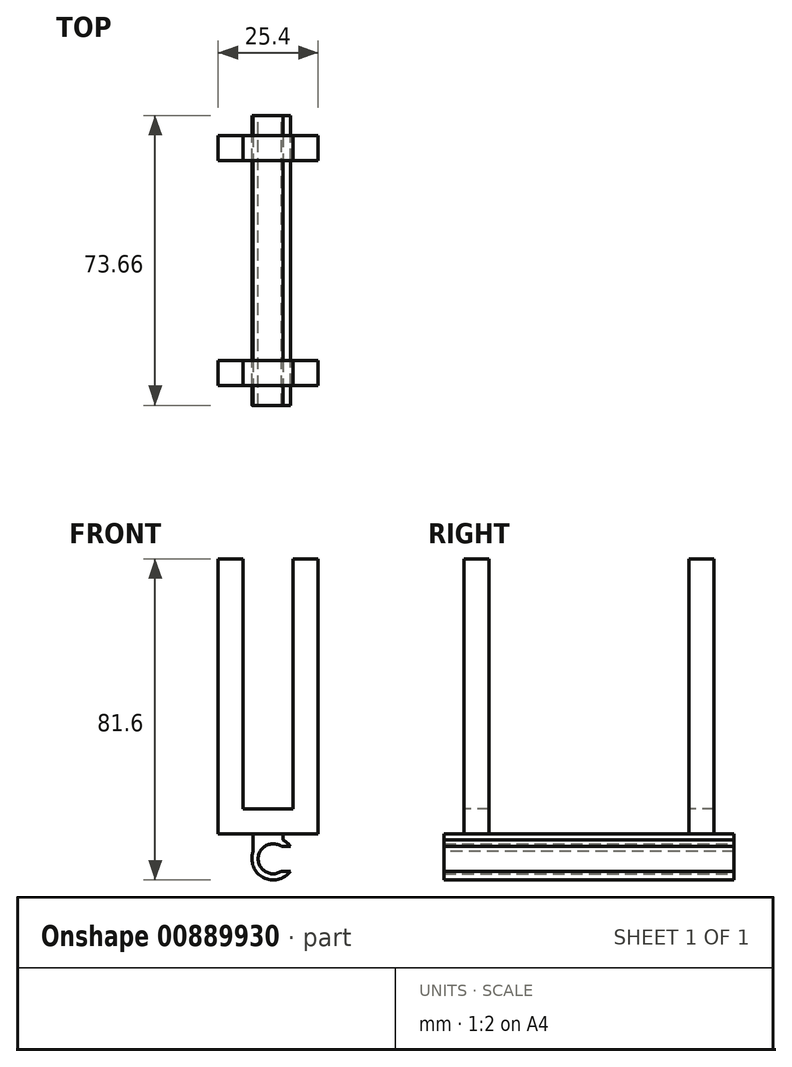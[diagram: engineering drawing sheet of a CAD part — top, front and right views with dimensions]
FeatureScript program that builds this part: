
annotation { "Feature Type Name" : "Feature", "Feature Type Description" : "" }
export const myFeature = defineFeature(function(context is Context, id is Id, definition is map)
    precondition{}
    {
        {
            var Q0;
            Q0=qCreatedBy(makeId("Front.planeOp"),FACE);
            var sketch = newSketch(context, id + "F0", { "sketchPlane" : qUnion([Q0])});
            skArc(sketch, "E0", {"start": v(2.1, 3.18) * mm, "mid": v(-3.81, 0) * mm, "end": v(2.1, -3.18) * mm});
            skArc(sketch, "E1.0", {"start": v(4.36, 3.18) * mm, "mid": v(-5.4, 0) * mm, "end": v(4.36, -3.18) * mm});
            skLineSegment(sketch, "E2", {"start": v(-5.4, 0) * mm, "end": v(5.4, 0) * mm, "construction": true});
            skLineSegment(sketch, "E3", {"start": v(-6.63, 3.18) * mm, "end": v(7.37, 3.18) * mm, "construction": true});
            skLineSegment(sketch, "E4", {"start": v(-6.34, -3.18) * mm, "end": v(7.33, -3.18) * mm, "construction": true});
            skLineSegment(sketch, "E5", {"start": v(2.1, 3.18) * mm, "end": v(4.36, 3.18) * mm});
            skLineSegment(sketch, "E6", {"start": v(2.1, -3.18) * mm, "end": v(4.36, -3.18) * mm});
            skPoint(sketch, "E6.startSnap0", {"position": v(0.5, -3.18) * mm});
            skSolve(sketch);
        }
        {
            var Q0;
            Q0 = qSketchRegion(id + "F0", true);
            extrude(context, id + "F1", {"entities" : qUnion([Q0]), "depth" : 73.66 * mm, "offsetDistance" : 25.4 * mm});
        }
        {
            var Q0;
            Q0=makeQuery(id+"F1.opExtrude","CAP_FACE",FACE,{"disambiguationData":[OSD([sQuery(id+"F0.wireOp",EDGE,"E0"),sQuery(id+"F0.wireOp",EDGE,"E1.0"),sQuery(id+"F0.wireOp",EDGE,"E5"),sQuery(id+"F0.wireOp",EDGE,"E6")])],"isStart":false});
            var sketch = newSketch(context, id + "F2", { "sketchPlane" : qUnion([Q0])});
            skLineSegment(sketch, "E7", {"start": v(-5.08, 1.82) * mm, "end": v(-5.08, 6.35) * mm});
            skLineSegment(sketch, "E8", {"start": v(2.54, 4.76) * mm, "end": v(2.54, 6.35) * mm});
            skLineSegment(sketch, "E9", {"start": v(2.54, 6.35) * mm, "end": v(-5.08, 6.35) * mm});
            skArc(sketch, "E10.0", {"start": v(2.54, 4.76) * mm, "mid": v(-1.94, 5.04) * mm, "end": v(-5.08, 1.82) * mm});
            skPoint(sketch, "E11.orphan", {"position": v(4.36, -3.18) * mm});
            skPoint(sketch, "E12.orphan", {"position": v(4.36, 3.18) * mm});
            skSolve(sketch);
        }
        {
            var Q0;
            Q0 = qSketchRegion(id + "F2", true);
            var Q1;
            Q1=makeQuery(id+"F1.opExtrude","CAP_FACE",FACE,{"disambiguationData":[OSD([sQuery(id+"F0.wireOp",EDGE,"E0"),sQuery(id+"F0.wireOp",EDGE,"E1.0"),sQuery(id+"F0.wireOp",EDGE,"E5"),sQuery(id+"F0.wireOp",EDGE,"E6")])],"isStart":true});
            extrude(context, id + "F3", {"entities" : qUnion([Q0]), "operationType" : NewBodyOperationType.ADD, "endBound" : BoundingType.UP_TO_SURFACE, "oppositeDirection" : true, "depth" : 25.4 * mm, "endBoundEntityFace" : qUnion([Q1]), "offsetDistance" : 25.4 * mm});
        }
        {
            var Q0;
            Q0=makeQuery(id+"F3.opExtrude","SWEPT_FACE",FACE,{"disambiguationData":[OSD([sQuery(id+"F2.wireOp",EDGE,"E9")])]});
            var sketch = newSketch(context, id + "F4", { "sketchPlane" : qUnion([Q0])});
            skLineSegment(sketch, "E13", {"start": v(-5.08, -36.83) * mm, "end": v(2.54, -36.83) * mm, "construction": true});
            skLineSegment(sketch, "E14", {"start": v(-13.97, -68.58) * mm, "end": v(11.43, -68.58) * mm});
            skLineSegment(sketch, "E15", {"start": v(-1.27, -73.66) * mm, "end": v(-1.27, 0) * mm, "construction": true});
            skLineSegment(sketch, "E16", {"start": v(-13.97, -68.58) * mm, "end": v(-13.97, -5.08) * mm, "construction": true});
            skLineSegment(sketch, "E17", {"start": v(-13.97, -5.08) * mm, "end": v(11.43, -5.08) * mm});
            skLineSegment(sketch, "E18", {"start": v(11.43, -5.08) * mm, "end": v(11.43, -68.58) * mm, "construction": true});
            skLineSegment(sketch, "E19.0", {"start": v(-13.97, -11.43) * mm, "end": v(11.43, -11.43) * mm});
            skLineSegment(sketch, "E20", {"start": v(-13.97, -5.08) * mm, "end": v(-13.97, -11.43) * mm});
            skLineSegment(sketch, "E21", {"start": v(11.43, -5.08) * mm, "end": v(11.43, -11.43) * mm});
            skLineSegment(sketch, "E22.0", {"start": v(-13.97, -62.23) * mm, "end": v(11.43, -62.23) * mm});
            skLineSegment(sketch, "E23", {"start": v(11.43, -62.23) * mm, "end": v(11.43, -68.58) * mm});
            skLineSegment(sketch, "E24", {"start": v(-13.97, -62.23) * mm, "end": v(-13.97, -68.58) * mm});
            skSolve(sketch);
        }
        {
            var Q0;
            Q0 = qSketchRegion(id + "F4", true);
            extrude(context, id + "F5", {"entities" : qUnion([Q0]), "operationType" : NewBodyOperationType.ADD, "depth" : 69.85 * mm, "offsetDistance" : 25.4 * mm});
        }
        {
            var Q0;
            Q0=makeQuery(id+"F5.opExtrude","SWEPT_FACE",FACE,{"disambiguationData":[OSD([sQuery(id+"F4.wireOp",EDGE,"E14")])]});
            var sketch = newSketch(context, id + "F6", { "sketchPlane" : qUnion([Q0])});
            skLineSegment(sketch, "E25", {"start": v(-1.27, 76.2) * mm, "end": v(-1.27, -11.05) * mm, "construction": true});
            skLineSegment(sketch, "E26.0", {"start": v(-7.62, 76.2) * mm, "end": v(-7.62, 12.7) * mm});
            skLineSegment(sketch, "E27.0", {"start": v(5.08, 76.2) * mm, "end": v(5.08, 12.7) * mm});
            skLineSegment(sketch, "E28", {"start": v(-7.62, 12.7) * mm, "end": v(5.08, 12.7) * mm});
            skLineSegment(sketch, "E29", {"start": v(-7.62, 76.2) * mm, "end": v(5.08, 76.2) * mm});
            skSolve(sketch);
        }
        {
            var Q0;
            Q0 = qSketchRegion(id + "F6", true);
            var Q1;
            Q1=makeQuery(id+"F5.opExtrude","SWEPT_FACE",FACE,{"disambiguationData":[OSD([sQuery(id+"F4.wireOp",EDGE,"E17")])]});
            extrude(context, id + "F7", {"entities" : qUnion([Q0]), "operationType" : NewBodyOperationType.REMOVE, "endBound" : BoundingType.UP_TO_SURFACE, "oppositeDirection" : true, "depth" : 25.4 * mm, "endBoundEntityFace" : qUnion([Q1]), "offsetDistance" : 25.4 * mm});
        }
    });
